# Revit family: 635-00-001 DN300
name_source: partatom
category: Pipe Accessories
units: mm (PartAtom-declared; Revit-internal decimal feet)

## family parameters
Always vertical = No
Cut with Voids When Loaded = No
Part Type = Valve - Breaks Into
Round Connector Dimension = Use Diameter
Shared = No
Work Plane-Based = No

## types (1)
- DN0300_PN16_OD_315
    1 = 1 mm  [stored 0.00328084 ft]
    10 = 10 mm  [stored 0.0328084 ft]
    12 = 11 mm  [stored 0.0360892 ft]
    2 = 2 mm  [stored 0.00656168 ft]
    25 = 40 mm  [stored 0.131234 ft]
    4 = 4 mm  [stored 0.0131234 ft]
    Bolt_End_dis = 104 mm
    Bore = 150 mm  [stored 0.492126 ft]
    Cap_Radius = 43.2 mm  [stored 0.141732 ft]
    D = 272.5 mm  [stored 0.894029 ft]
    D1 = 231.63 mm
    D2 = 172.7 mm  [stored 0.566601 ft]
    D3 = 81.75 mm
    DN = 300 mm  [stored 0.984252 ft]
    DN0300_PN16_OD_315 = 635-356-00-166
    Default Elevation = 0 mm  [stored 0 ft]
    Description_ = AVK SUPA MAXI™ TRANSITION COUPLING, PE100/PN16
    FL_T = 70 mm  [stored 0.229659 ft]
    FL_T2 = 35 mm  [stored 0.114829 ft]
    FLange_T1 = 114.4 mm
    L = 784 mm  [stored 2.57218 ft]
    L1 = 315 mm  [stored 1.03346 ft]
    L3 = 235.2 mm  [stored 0.771654 ft]
    L4 = 258.72 mm  [stored 0.848819 ft]
    L4-L3 = 16.46 mm
    L5 = 323.4 mm  [stored 1.06102 ft]
    OD = 157.5 mm  [stored 0.516732 ft]
    PCD = 221.63 mm
    PCD1 = 50.88 mm
    Ring_Dia = 191 mm  [stored 0.62664 ft]
    Ring_Dia1 = 175.72 mm  [stored 0.576509 ft]
    Ring_dia2 = 166.61 mm
    Ring_dia3 = 183.27 mm
    Ring_dis = 400 mm  [stored 1.31234 ft]
    SR1 = 157 mm  [stored 0.515092 ft]
    SR2 = 178 mm  [stored 0.58399 ft]
    Search_table = 635-00-001 DN300
    Thickness = 31.5 mm  [stored 0.103346 ft]
    URL product pages = https://www.avkvalves.com

note: [stored X ft] marks values corroborated as IEEE doubles in the binary element streams (Revit-internal decimal feet)

## geometry (parser evidence)
native form markers: Sweep x4
no freeform markers — native parametric forms only
